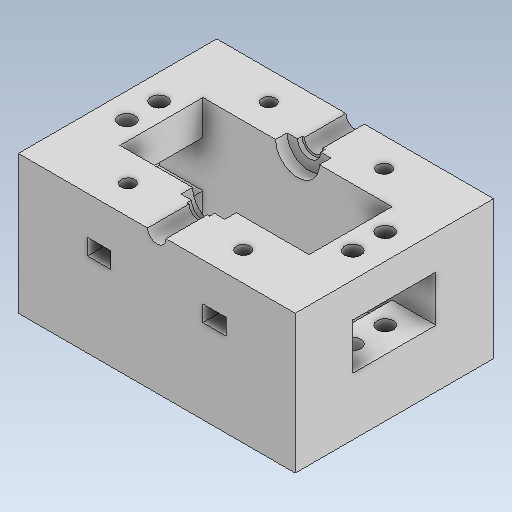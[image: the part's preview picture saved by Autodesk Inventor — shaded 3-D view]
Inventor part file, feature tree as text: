
AUTODESK INVENTOR PART (.ipt)
format: ipt  version: 2020.2 (Build 242310000, 310)  size: 412,160 bytes
history: native  units: mm
features: sketch x15, extrude x13, other x3, hole x2, reference x1
ambient origin geometry x8: Origin, YZ Plane, XZ Plane, XY Plane, X Axis, Y Axis, Z Axis, Center Point
bodies: Solido1 (feature_tree)
feature tree (34):
  extrude  "Estrusione1"  Depth=120.0mm
  extrude  "Estrusione2"  Depth=86.0mm
  extrude  "Estrusione3"  Depth=60.0mm TaperAngle=0.0deg
  extrude  "Estrusione4"  Depth=15.0mm
  extrude  "Estrusione5"  Depth=36.0mm
  extrude  "Estrusione6"  Depth=30.0mm
  hole  "Foro1"  [1 undecoded]
  extrude  "Estrusione7"  Depth=19.0mm
  extrude  "Estrusione8"  Depth=5.0mm TaperAngle=0.0deg
  sketch  "Schizzo12"
  extrude  "Estrusione9"  Depth=8.0mm
  extrude  "Estrusione11"  Depth=20.0mm TaperAngle=0.0deg
  extrude  "Estrusione12"  Depth=19.0mm
  extrude  "Estrusione14"  Depth=5.0mm TaperAngle=0.0deg
  hole  "Foro5"  [1 undecoded]
  extrude  "Estrusione15"  Depth=50.0mm
  sketch  "Schizzo1"
  sketch  "Schizzo2"
  sketch  "Schizzo3"
  sketch  "Schizzo4"
  sketch  "Schizzo5"
  sketch  "Schizzo6"
  sketch  "Schizzo7"
  sketch  "Schizzo8"
  sketch  "Schizzo10"
  sketch  "Schizzo13"
  sketch  "Schizzo16"
  sketch  "Schizzo17"
  sketch  "Schizzo21"
  sketch  "Schizzo22"
  reference  "Riferimento1"
  other  "<userpath>\Desktop\mv-Project\04_PartDraw\Pendolo_Inverso.iam"
  other  "Pendolo_Inverso.iam"
  other  "20_Base_Sopra:2"
note: 2 required parameter values undecoded (feature->parameter linkage not recoverable at this tier; creation-order binding heuristic only, values carry confidence <= 0.55)
